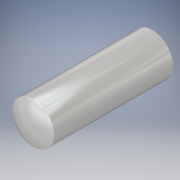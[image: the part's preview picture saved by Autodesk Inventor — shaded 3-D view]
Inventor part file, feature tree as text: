
AUTODESK INVENTOR PART (.ipt)
format: ipt  version: 2017 (Build 210142000, 142)  size: 112,640 bytes
history: native  units: in
note: dims shown in document units (in); Inventor stores cm internally (conversion verified against a paired STEP export)
features: sketch x2, extrude x1, revolve x1
ambient origin geometry x8: Origin, YZ Plane, XZ Plane, XY Plane, X Axis, Y Axis, Z Axis, Center Point
bodies: Solid1 (feature_tree)
feature tree (4):
  extrude  "Extrusion1"  Depth=0.1181in TaperAngle=0.0deg
  revolve  "Revolution1"  [1 undecoded]
  sketch  "Sketch1"  dims[d0=0.1181in d1=0.3543in d2=0.0in]
  sketch  "Sketch2"  dims[d3=0.2362in d4=0.1181in d5=180.0deg]
note: 1 required parameter value undecoded (feature->parameter linkage not recoverable at this tier; creation-order binding heuristic only, values carry confidence <= 0.55)
